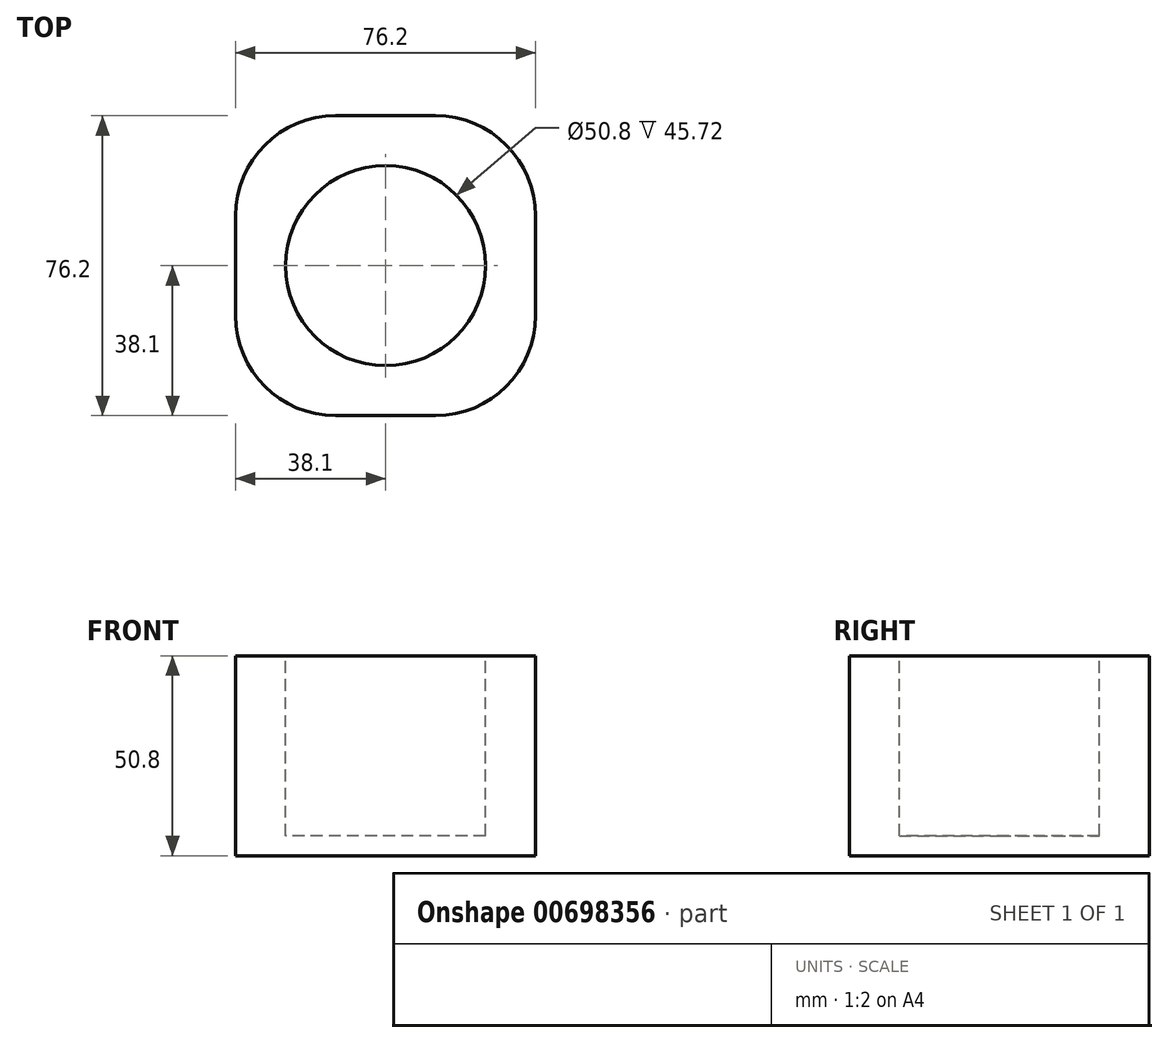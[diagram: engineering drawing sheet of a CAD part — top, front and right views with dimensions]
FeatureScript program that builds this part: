
annotation { "Feature Type Name" : "Feature", "Feature Type Description" : "" }
export const myFeature = defineFeature(function(context is Context, id is Id, definition is map)
    precondition{}
    {
        {
            var Q0;
            Q0=qCreatedBy(makeId("Top.planeOp"),FACE);
            var sketch = newSketch(context, id + "F0", { "sketchPlane" : qUnion([Q0])});
            skLineSegment(sketch, "E0.bottom", {"start": v(38.1, 38.1) * mm, "end": v(-38.1, 38.1) * mm});
            skLineSegment(sketch, "E0.top", {"start": v(38.1, -38.1) * mm, "end": v(-38.1, -38.1) * mm});
            skLineSegment(sketch, "E0.left", {"start": v(38.1, 38.1) * mm, "end": v(38.1, -38.1) * mm});
            skLineSegment(sketch, "E0.right", {"start": v(-38.1, 38.1) * mm, "end": v(-38.1, -38.1) * mm});
            skPoint(sketch, "E0.middle", {"position": v(0, 0) * mm});
            skSolve(sketch);
        }
        {
            var Q0;
            Q0 = qSketchRegion(id + "F0", true);
            extrude(context, id + "F1", {"entities" : qUnion([Q0]), "depth" : 50.8 * mm, "offsetDistance" : 25.4 * mm});
        }
        {
            var Q0;
            Q0=makeQuery(id+"F1.opExtrude","SWEPT_EDGE",EDGE,{"disambiguationData":[OSD([sQuery(id+"F0.wireOp",EDGE,"E0.top"),sQuery(id+"F0.wireOp",EDGE,"E0.right")])]});
            var Q1;
            Q1=makeQuery(id+"F1.opExtrude","SWEPT_EDGE",EDGE,{"disambiguationData":[OSD([sQuery(id+"F0.wireOp",EDGE,"E0.top"),sQuery(id+"F0.wireOp",EDGE,"E0.left")])]});
            var Q2;
            Q2=makeQuery(id+"F1.opExtrude","SWEPT_EDGE",EDGE,{"disambiguationData":[OSD([sQuery(id+"F0.wireOp",EDGE,"E0.bottom"),sQuery(id+"F0.wireOp",EDGE,"E0.right")])]});
            var Q3;
            Q3=makeQuery(id+"F1.opExtrude","SWEPT_EDGE",EDGE,{"disambiguationData":[OSD([sQuery(id+"F0.wireOp",EDGE,"E0.bottom"),sQuery(id+"F0.wireOp",EDGE,"E0.left")])]});
            fillet(context, id + "F2", {"entities" : qUnion([Q0, Q1, Q2, Q3]), "radius" : 25.4 * mm, "tangentPropagation" : true, "allowEdgeOverflow" : false});
        }
        {
            var Q0;
            Q0=makeQuery(id+"F1.opExtrude","CAP_FACE",FACE,{"disambiguationData":[OSD([sQuery(id+"F0.wireOp",EDGE,"E0.bottom"),sQuery(id+"F0.wireOp",EDGE,"E0.top"),sQuery(id+"F0.wireOp",EDGE,"E0.left"),sQuery(id+"F0.wireOp",EDGE,"E0.right")])],"isStart":false});
            var sketch = newSketch(context, id + "F3", { "sketchPlane" : qUnion([Q0])});
            skCircle(sketch, "E1", {"center": v(0, 0) * mm, "radius": 25.4 * mm});
            skSolve(sketch);
        }
        {
            var Q0;
            Q0 = qSketchRegion(id + "F3", true);
            extrude(context, id + "F4", {"entities" : qUnion([Q0]), "operationType" : NewBodyOperationType.REMOVE, "oppositeDirection" : true, "depth" : 45.72 * mm, "offsetDistance" : 25.4 * mm});
        }
    });
